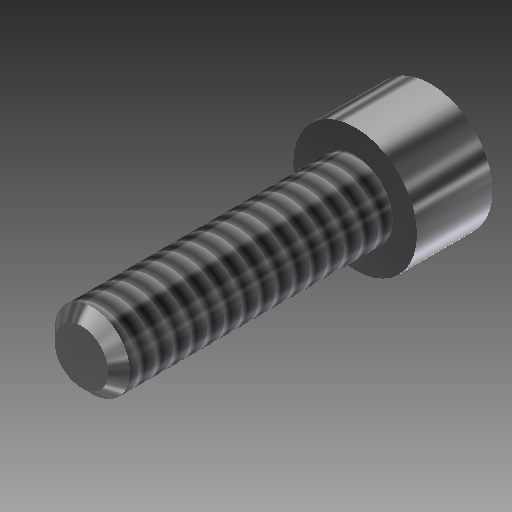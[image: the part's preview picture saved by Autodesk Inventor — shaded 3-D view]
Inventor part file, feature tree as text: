
AUTODESK INVENTOR PART (.ipt)
format: ipt  version: 2019 (Build 230136000, 136)  size: 179,200 bytes
history: native  units: in
note: dims shown in document units (in); Inventor stores cm internally (conversion verified against a paired STEP export)
features: extrude x3, sketch x3, thread x1, chamfer x1
ambient origin geometry x8: Origin, YZ Plane, XZ Plane, XY Plane, X Axis, Y Axis, Z Axis, Center Point
bodies: Solid1 (feature_tree)
feature tree (8):
  extrude  "Extrusion1"  Depth=0.5in TaperAngle=0.0deg
  extrude  "Extrusion2"  Depth=0.138in TaperAngle=0.0deg
  extrude  "Extrusion3"  Depth=0.069in TaperAngle=0.0deg
  thread  "Thread1"  [1 undecoded]
  chamfer  "Chamfer1"  Distance=0.02in Angle=45.0deg
  sketch  "Sketch1"  dims[d0=0.138in d1=0.5in d2=0.0in]
  sketch  "Sketch2"  dims[d3=0.226in d4=0.138in d5=0.0in]
  sketch  "Sketch3"  dims[d6=0.1094in d7=0.069in d8=0.0in d9=1.0in d10=0.0in d11=0.02in d12=0.125in d13=45.0deg]
note: 1 required parameter value undecoded (feature->parameter linkage not recoverable at this tier; creation-order binding heuristic only, values carry confidence <= 0.55)
